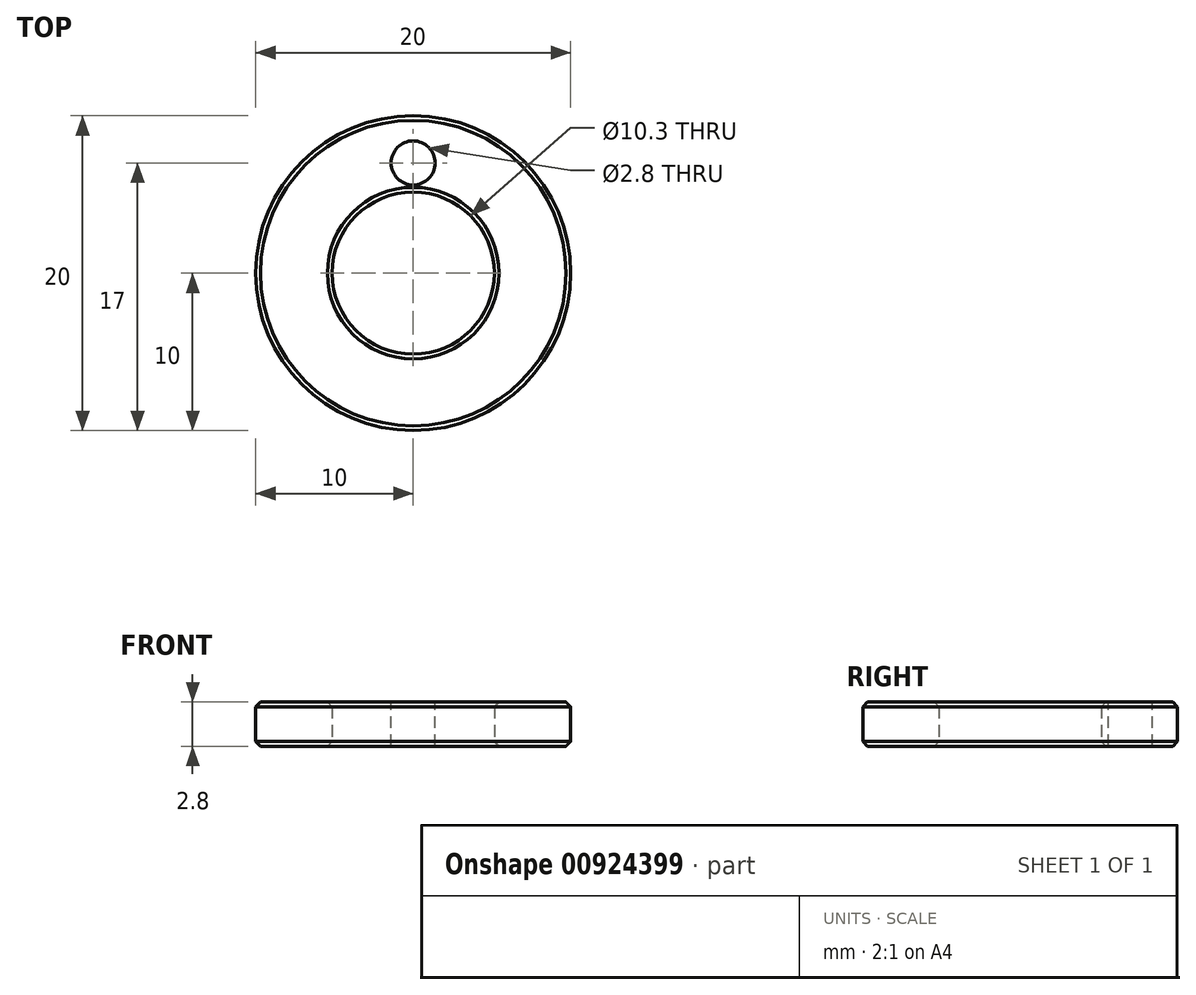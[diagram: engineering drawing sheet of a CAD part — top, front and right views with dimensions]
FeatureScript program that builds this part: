
annotation { "Feature Type Name" : "Feature", "Feature Type Description" : "" }
export const myFeature = defineFeature(function(context is Context, id is Id, definition is map)
    precondition{}
    {
        {
            var Q0;
            Q0=qCreatedBy(makeId("Top.planeOp"),FACE);
            var sketch = newSketch(context, id + "F0", { "sketchPlane" : qUnion([Q0])});
            skCircle(sketch, "E0", {"center": v(0, 0) * mm, "radius": 10 * mm});
            skCircle(sketch, "E1", {"center": v(0, 0) * mm, "radius": 5.15 * mm});
            skSolve(sketch);
        }
        {
            var Q0;
            Q0 = qSketchRegion(id + "F0", true);
            extrude(context, id + "F1", {"entities" : qUnion([Q0]), "depth" : 2.8 * mm, "offsetDistance" : 25 * mm});
        }
        {
            var Q0;
            Q0=makeQuery(id+"F1.opExtrude","CAP_FACE",FACE,{"disambiguationData":[OSD([sQuery(id+"F0.wireOp",EDGE,"E0"),sQuery(id+"F0.wireOp",EDGE,"E1")])],"isStart":false});
            var sketch = newSketch(context, id + "F2", { "sketchPlane" : qUnion([Q0])});
            skPoint(sketch, "E2", {"position": v(0, 7) * mm});
            skCircle(sketch, "E3", {"center": v(0, 0) * mm, "radius": 7 * mm, "construction": true});
            skSolve(sketch);
        }
        {
            var Q0;
            Q0=sQuery(id+"F2.wireOp",VERTEX,"E2");
            var Q1;
            Q1=makeQuery(id+"F1.opExtrude","SWEPT_BODY",BODY,{"disambiguationData":[OSD([sQuery(id+"F0.wireOp",EDGE,"E0"),sQuery(id+"F0.wireOp",EDGE,"E1")])]});
            hole(context, id + "F3", {"style" : HoleStyle.SIMPLE, "endStyle" : HoleEndStyle.THROUGH, "holeDiameter" : 2.8 * mm, "majorDiameter" : 5 * mm, "isTappedThrough" : true, "tappedDepth" : 12 * mm, "tapClearance" : 3, "locations" : qUnion([Q0]), "scope" : qUnion([Q1])});
        }
        {
            var Q0;
            Q0=makeQuery(id+"F1.opExtrude","CAP_EDGE",EDGE,{"disambiguationData":[OSD([sQuery(id+"F0.wireOp",EDGE,"E1")])],"isStart":true});
            var Q1;
            Q1=makeQuery(id+"F1.opExtrude","CAP_EDGE",EDGE,{"disambiguationData":[OSD([sQuery(id+"F0.wireOp",EDGE,"E0")])],"isStart":true});
            var Q2;
            Q2=makeQuery(id+"F1.opExtrude","CAP_EDGE",EDGE,{"disambiguationData":[OSD([sQuery(id+"F0.wireOp",EDGE,"E1")])],"isStart":false});
            var Q3;
            Q3=makeQuery(id+"F1.opExtrude","CAP_EDGE",EDGE,{"disambiguationData":[OSD([sQuery(id+"F0.wireOp",EDGE,"E0")])],"isStart":false});
            chamfer(context, id + "F4", {"entities" : qUnion([Q0, Q1, Q2, Q3]), "width" : 0.3 * mm, "tangentPropagation" : true});
        }
    });
